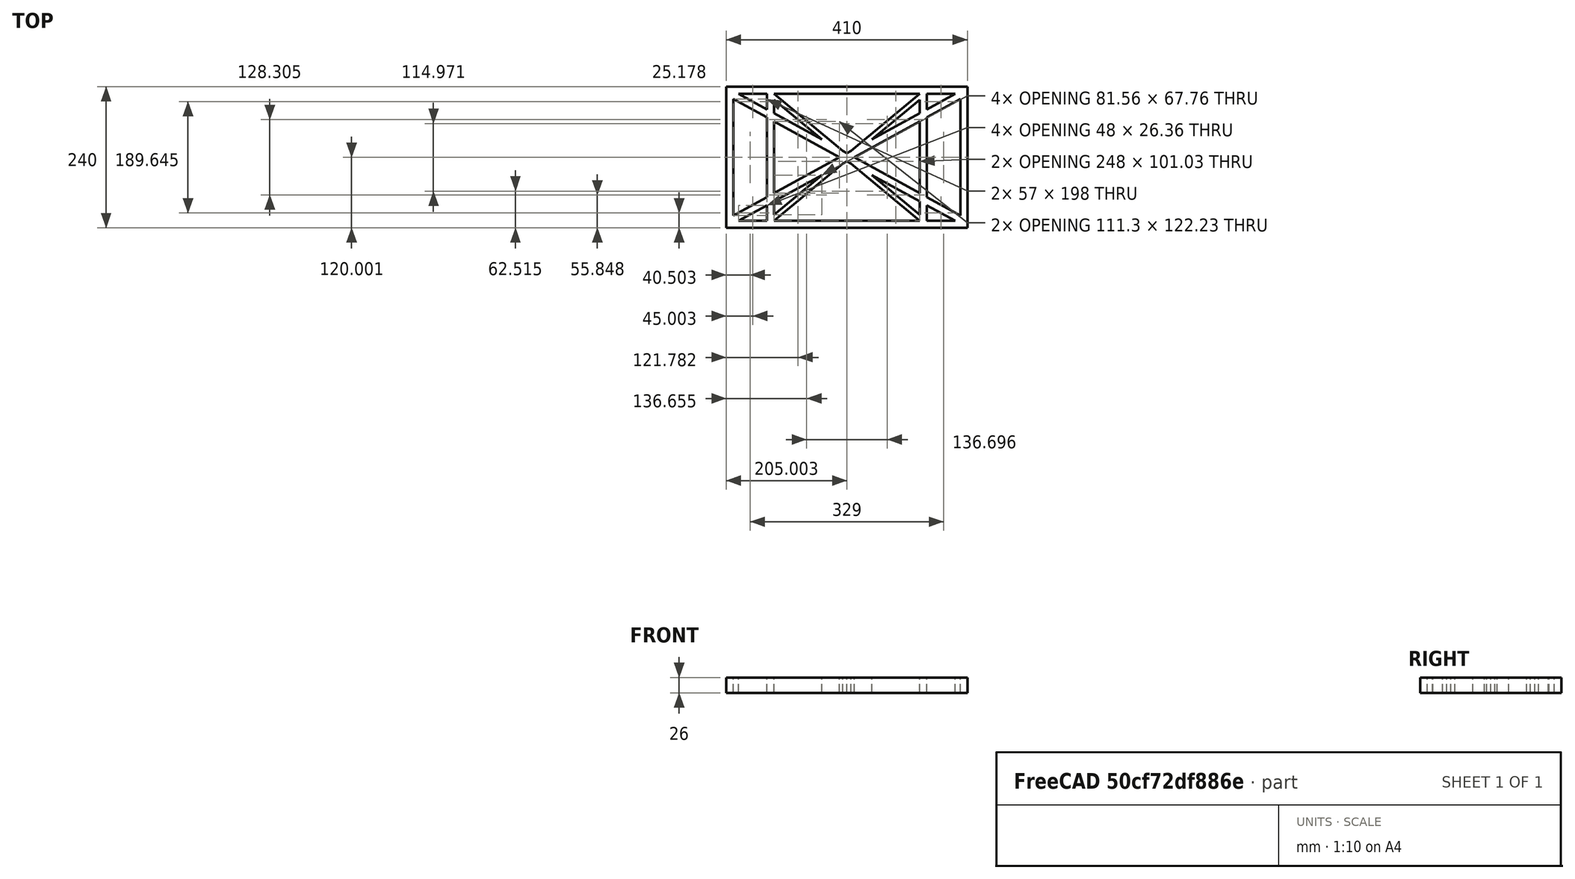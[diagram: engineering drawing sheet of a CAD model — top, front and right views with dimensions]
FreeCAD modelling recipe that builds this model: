
FCSTD DOCUMENT  (FreeCAD 0.19R0.19.2)
Label: laptopStand022
License: All rights reserved
LicenseURL: http://en.wikipedia.org/wiki/All_rights_reserved
objects: Sketcher::SketchObject×3, Part::Extrusion×1
note: 4 computed .brp shape members not serialized (recipe doc carries the construction recipe); baked Part::Feature solids carry a one-line shape summary decoded from their .brp

FEATURE [Sketcher::SketchObject] Sketch
  FullyConstrained = true
  sketch-geometry (52):
    g0: LineSegment StartX=-22.9272 StartY=136.221 StartZ=0 EndX=-22.9272 EndY=-103.779 EndZ=0
    g1: LineSegment StartX=-22.9272 StartY=136.221 StartZ=0 EndX=387.073 EndY=136.221 EndZ=0
    g2: LineSegment StartX=-22.9272 StartY=-103.779 StartZ=0 EndX=387.073 EndY=-103.779 EndZ=0
    g3: LineSegment StartX=387.073 StartY=136.221 StartZ=0 EndX=387.073 EndY=-103.779 EndZ=0
    g4: LineSegment StartX=375.073 StartY=115.221 StartZ=0 EndX=318.073 EndY=83.9235 EndZ=0
    g5: LineSegment StartX=-10.9272 StartY=-82.7794 StartZ=0 EndX=46.0728 EndY=-51.4823 EndZ=0
    g6: LineSegment StartX=-1.92719 StartY=124.221 StartZ=0 EndX=46.0728 EndY=97.8651 EndZ=0
    g7: LineSegment StartX=366.073 StartY=-91.7794 StartZ=0 EndX=318.073 EndY=-65.424 EndZ=0
    g8: LineSegment StartX=-10.9272 StartY=115.221 StartZ=0 EndX=-10.9272 EndY=-82.7794 EndZ=0
    g9: LineSegment StartX=375.073 StartY=-82.7794 StartZ=0 EndX=375.073 EndY=115.221 EndZ=0
    g10: LineSegment StartX=-1.92719 StartY=-91.7794 StartZ=0 EndX=46.0728 EndY=-91.7794 EndZ=0
    g11: LineSegment StartX=318.073 StartY=124.221 StartZ=0 EndX=366.073 EndY=124.221 EndZ=0
    g12: LineSegment StartX=306.073 StartY=-81.8102 StartZ=0 EndX=224.513 EndY=-14.0532 EndZ=0
    g13: LineSegment StartX=58.0728 StartY=114.251 StartZ=0 EndX=139.632 EndY=46.4944 EndZ=0
    g14: LineSegment StartX=306.073 StartY=124.221 StartZ=0 EndX=189.124 EndY=27.0628 EndZ=0
    g15: LineSegment StartX=58.0728 StartY=-91.7794 StartZ=0 EndX=175.022 EndY=5.37834 EndZ=0
    g16: LineSegment StartX=46.0728 StartY=124.221 StartZ=0 EndX=46.0728 EndY=97.8651 EndZ=0
    g17: LineSegment StartX=58.0728 StartY=-81.8102 StartZ=0 EndX=58.0728 EndY=-58.8351 EndZ=0
    g18: LineSegment StartX=318.073 StartY=124.221 StartZ=0 EndX=318.073 EndY=97.8651 EndZ=0
    g19: LineSegment StartX=306.073 StartY=114.251 StartZ=0 EndX=306.073 EndY=91.2763 EndZ=0
    g20: LineSegment StartX=182.073 StartY=23.1914 StartZ=0 EndX=189.124 EndY=27.0628 EndZ=0
    g21: LineSegment StartX=182.073 StartY=9.24976 StartZ=0 EndX=175.022 EndY=5.37834 EndZ=0
    g22: LineSegment StartX=224.513 StartY=46.4944 StartZ=0 EndX=306.073 EndY=114.251 EndZ=0
    g23: LineSegment StartX=175.022 StartY=27.0628 StartZ=0 EndX=58.0728 EndY=124.221 EndZ=0
    g24: LineSegment StartX=169.377 StartY=16.2206 StartZ=0 EndX=58.0728 EndY=77.3346 EndZ=0
    g25: LineSegment StartX=139.632 StartY=-14.0532 StartZ=0 EndX=58.0728 EndY=-81.8102 EndZ=0
    g26: LineSegment StartX=194.768 StartY=16.2206 StartZ=0 EndX=306.073 EndY=-44.8935 EndZ=0
    g27: LineSegment StartX=224.513 StartY=46.4944 StartZ=0 EndX=306.073 EndY=91.2763 EndZ=0
    g28: LineSegment StartX=175.022 StartY=27.0628 StartZ=0 EndX=182.073 EndY=23.1914 EndZ=0
    g29: LineSegment StartX=139.632 StartY=-14.0532 StartZ=0 EndX=58.0728 EndY=-58.8351 EndZ=0
    g30: LineSegment StartX=189.124 StartY=5.37834 StartZ=0 EndX=182.073 EndY=9.24976 EndZ=0
    g31: LineSegment StartX=189.124 StartY=5.37834 StartZ=0 EndX=306.073 EndY=-91.7794 EndZ=0
    g32: LineSegment StartX=306.073 StartY=77.3346 StartZ=0 EndX=306.073 EndY=-44.8935 EndZ=0
    g33: LineSegment StartX=318.073 StartY=83.9235 StartZ=0 EndX=318.073 EndY=-51.4823 EndZ=0
    g34: LineSegment StartX=318.073 StartY=97.8651 StartZ=0 EndX=366.073 EndY=124.221 EndZ=0
    g35: LineSegment StartX=306.073 StartY=77.3346 StartZ=0 EndX=194.768 EndY=16.2206 EndZ=0
    g36: LineSegment StartX=306.073 StartY=-58.8351 StartZ=0 EndX=224.513 EndY=-14.0532 EndZ=0
    g37: LineSegment StartX=306.073 StartY=-58.8351 StartZ=0 EndX=306.073 EndY=-81.8102 EndZ=0
    g38: LineSegment StartX=318.073 StartY=-51.4823 StartZ=0 EndX=375.073 EndY=-82.7794 EndZ=0
    g39: LineSegment StartX=318.073 StartY=-65.424 StartZ=0 EndX=318.073 EndY=-91.7794 EndZ=0
    g40: LineSegment StartX=306.073 StartY=124.221 StartZ=0 EndX=58.0728 EndY=124.221 EndZ=0
    g41: LineSegment StartX=318.073 StartY=-91.7794 StartZ=0 EndX=366.073 EndY=-91.7794 EndZ=0
    g42: LineSegment StartX=58.0728 StartY=-91.7794 StartZ=0 EndX=306.073 EndY=-91.7794 EndZ=0
    g43: LineSegment StartX=58.0728 StartY=-44.8935 StartZ=0 EndX=58.0728 EndY=77.3346 EndZ=0
    g44: LineSegment StartX=46.0728 StartY=-65.424 StartZ=0 EndX=-1.92719 EndY=-91.7794 EndZ=0
    g45: LineSegment StartX=46.0728 StartY=-65.424 StartZ=0 EndX=46.0728 EndY=-91.7794 EndZ=0
    g46: LineSegment StartX=58.0728 StartY=-44.8935 StartZ=0 EndX=169.377 EndY=16.2206 EndZ=0
    g47: LineSegment StartX=58.0728 StartY=91.2763 StartZ=0 EndX=58.0728 EndY=114.251 EndZ=0
    g48: LineSegment StartX=46.0728 StartY=83.9235 StartZ=0 EndX=46.0728 EndY=-51.4823 EndZ=0
    g49: LineSegment StartX=46.0728 StartY=124.221 StartZ=0 EndX=-1.92719 EndY=124.221 EndZ=0
    g50: LineSegment StartX=58.0728 StartY=91.2763 StartZ=0 EndX=139.632 EndY=46.4944 EndZ=0
    g51: LineSegment StartX=46.0728 StartY=83.9235 StartZ=0 EndX=-10.9272 EndY=115.221 EndZ=0
  constraints (102):
    c: Vertical(g0)
    c: Distance(g0) = 240
    c: Horizontal(g1)
    c: Distance(g1) = 410
    c: Coincident(g1,g0)
    c: Coincident(g2,g0)
    c: Horizontal(g2)
    c: Coincident(g3,g1)
    c: Vertical(g3)
    c: Coincident(g2,g3)
    c: Block(g1)
    c: Horizontal(g10)
    c: Horizontal(g11)
    c: PointOnObject(g35,g6)
    c: Coincident(g28,g20)
    c: Coincident(g30,g21)
    c: Tangent(g7,g24)
    c: PointOnObject(g24,g5)
    c: PointOnObject(g26,g4)
    c: Coincident(g20,g14)
    c: Tangent(g20,g27)
    c: Coincident(g50,g13)
    c: Coincident(g28,g23)
    c: Coincident(g22,g27)
    c: Coincident(g21,g15)
    c: Coincident(g29,g25)
    c: Tangent(g21,g29)
    c: Coincident(g36,g12)
    c: Coincident(g31,g30)
    c: Coincident(g22,g19)
    c: Tangent(g19,g32)
    c: Tangent(g18,g33)
    c: Coincident(g27,g19)
    c: Tangent(g27,g34)
    c: Coincident(g4,g33)
    c: Coincident(g35,g32)
    c: Tangent(g4,g35)
    c: Coincident(g37,g12)
    c: Tangent(g7,g36)
    c: Tangent(g32,g37)
    c: Coincident(g26,g32)
    c: Tangent(g26,g38)
    c: Coincident(g33,g38)
    c: Coincident(g39,g7)
    c: Tangent(g33,g39)
    c: Coincident(g25,g17)
    c: Tangent(g17,g43)
    c: Coincident(g29,g17)
    c: Tangent(g29,g44)
    c: Coincident(g45,g44)
    c: Tangent(g16,g45)
    c: Coincident(g5,g48)
    c: Coincident(g46,g43)
    c: Tangent(g5,g46)
    c: Tangent(g43,g47)
    c: Tangent(g16,g48)
    c: Coincident(g13,g47)
    c: PointOnObject(g40,g23)
    c: Tangent(g40,g49)
    c: Coincident(g6,g16)
    c: Coincident(g50,g47)
    c: Tangent(g6,g50)
    c: Coincident(g24,g43)
    c: Coincident(g51,g48)
    c: Tangent(g24,g51)
    c: Block(g23)
    c: Block(g14)
    c: Block(g20)
    c: Block(g40)
    c: Block(g18)
    c: Block(g34)
    c: Block(g4)
    c: Block(g38)
    c: Block(g9)
    c: Block(g36)
    c: Block(g37)
    c: Block(g7)
    c: Block(g39)
    c: Block(g22)
    c: Block(g31)
    c: Block(g42)
    c: Block(g21)
    c: Block(g15)
    c: Block(g29)
    c: Block(g25)
    c: Block(g45)
    c: Block(g44)
    c: Block(g5)
    c: Block(g8)
    c: Block(g51)
    c: Block(g6)
    c: Block(g16)
    c: Block(g13)
    c: Block(g47)
    c: Block(g35)
    c: Block(g32)
    c: Block(g24)
    c: Block(g46)
    c: Block(g49)
    c: Block(g11)
    c: Block(g41)
    c: Block(g10)
FEATURE [Part::Extrusion] Extrude
  Base = -> Sketch
  Dir = (0,0,1)
  DirMode = 2
  FaceMakerClass = Part::FaceMakerBullseye
  LengthFwd = 26
  LengthRev = 0
  Solid = true
  Symmetric = false
FEATURE [Sketcher::SketchObject] Sketch001
  FullyConstrained = false
  MapMode = 4
  Placement = pos=(0,0,0) rot=(0.57735,0.57735,0.57735;2.0944rad)
  Support = -> [Sketch]
  sketch-geometry (23):
    g0: LineSegment StartX=17.2228 StartY=-16.0875 StartZ=0 EndX=117.223 EndY=-16.0875 EndZ=0
    g1: LineSegment StartX=17.2228 StartY=-16.0875 StartZ=0 EndX=17.2228 EndY=-19.0875 EndZ=0
    g2: LineSegment StartX=117.223 StartY=-16.0875 StartZ=0 EndX=117.223 EndY=-19.0875 EndZ=0
    g3: BSplineCurve PolesCount=3 KnotsCount=2 Degree=2 IsPeriodic=0
    g4: LineSegment StartX=94.6577 StartY=-26.1351 StartZ=0 EndX=24.2583 EndY=-213.335 EndZ=0
    g5: LineSegment StartX=-9.4377 StartY=-200.664 StartZ=0 EndX=24.2583 EndY=-213.335 EndZ=0
    g6: LineSegment StartX=-9.4377 StartY=-200.664 StartZ=0 EndX=56.1962 EndY=-26.1351 EndZ=0
    g7: LineSegment StartX=17.2228 StartY=-19.0875 StartZ=0 EndX=38.8094 EndY=-19.0875 EndZ=0
    g8: BSplineCurve PolesCount=4 KnotsCount=2 Degree=3 IsPeriodic=0
    g9: LineSegment StartX=56.1962 StartY=-26.1351 StartZ=0 EndX=58.7648 EndY=-19.3049 EndZ=0
    g10: LineSegment StartX=94.6577 StartY=-26.1351 StartZ=0 EndX=97.3081 EndY=-19.0875 EndZ=0
    g11: LineSegment StartX=58.7648 StartY=-19.3049 StartZ=0 EndX=78.0148 EndY=-19.3049 EndZ=0
    g12: LineSegment StartX=72.4029 StartY=-71.0782 StartZ=0 EndX=76.9849 EndY=-58.9235 EndZ=0
    g13: LineSegment StartX=60.2385 StartY=-66.4925 StartZ=0 EndX=72.4029 EndY=-71.0782 EndZ=0
    g14: LineSegment StartX=60.2385 StartY=-66.4925 StartZ=0 EndX=48.0742 EndY=-61.9068 EndZ=0
    g15: LineSegment StartX=48.0742 StartY=-61.9068 StartZ=0 EndX=52.6617 EndY=-49.7374 EndZ=0
    g16: LineSegment StartX=72.9373 StartY=-32.8066 StartZ=0 EndX=60.2385 EndY=-66.4925 EndZ=0
    g17: LineSegment StartX=72.9373 StartY=-32.8066 StartZ=0 EndX=85.1017 EndY=-37.3922 EndZ=0
    g18: LineSegment StartX=72.9373 StartY=-32.8066 StartZ=0 EndX=60.7729 EndY=-28.2209 EndZ=0
    g19: LineSegment StartX=85.1017 StartY=-37.3922 StartZ=0 EndX=80.516 EndY=-49.5566 EndZ=0
    g20: LineSegment StartX=60.7729 StartY=-28.2209 StartZ=0 EndX=56.1873 EndY=-40.3853 EndZ=0
    g21: LineSegment StartX=60.2385 StartY=-66.4925 StartZ=0 EndX=64.8242 EndY=-54.3281 EndZ=0
    g22: LineSegment StartX=72.9373 StartY=-32.8066 StartZ=0 EndX=68.3516 EndY=-44.9709 EndZ=0
  constraints (55):
    c: Horizontal(g0)
    c: Distance(g0) = 100
    c: Block(g0)
    c: Coincident(g1,g0)
    c: Vertical(g1)
    c: Distance(g1) = 3
    c: Coincident(g2,g0)
    c: Vertical(g2)
    c: Distance(g2) = 3
    c: Block(g3)
    c: Coincident(g3,g2)
    c: Coincident(g4,g3)
    c: Block(g4)
    c: Coincident(g5,g4)
    c: Coincident(g6,g5)
    c: Coincident(g7,g1)
    c: Horizontal(g7)
    c: Block(g8)
    c: Coincident(g8,g7)
    c: Coincident(g8,g6)
    c: Block(g6)
    c: Coincident(g9,g6)
    c: Coincident(g10,g3)
    c: Parallel(g10,g4)
    c: Coincident(g11,g9)
    c: Horizontal(g11)
    c: Distance(g11) = 19.25
    c: Block(g9)
    c: Coincident(g14,g16)
    c: Coincident(g13,g16)
    c: Coincident(g12,g13)
    c: Coincident(g15,g14)
    c: Coincident(g17,g16)
    c: Block(g13)
    c: Block(g14)
    c: Block(g16)
    c: Distance(g17) = 13
    c: Coincident(g18,g16)
    c: Distance(g18) = 13
    c: Perpendicular(g17,g16)
    c: Perpendicular(g18,g16)
    c: Coincident(g19,g17)
    c: Distance(g19) = 13
    c: Coincident(g20,g18)
    c: Distance(g20) = 13
    c: Perpendicular(g18,g20)
    c: Perpendicular(g17,g19)
    c: Perpendicular(g13,g12)
    c: Perpendicular(g15,g14)
    c: Distance(g21) = 13
    c: Distance(g22) = 13
    c: Parallel(g22,g16)
    c: Parallel(g16,g21)
    c: Coincident(g21,g13)
    c: Coincident(g22,g16)
FEATURE [Sketcher::SketchObject] Sketch002
  FullyConstrained = true
  Placement = pos=(0,0,0) rot=(-1,0,0;4.71239rad)
